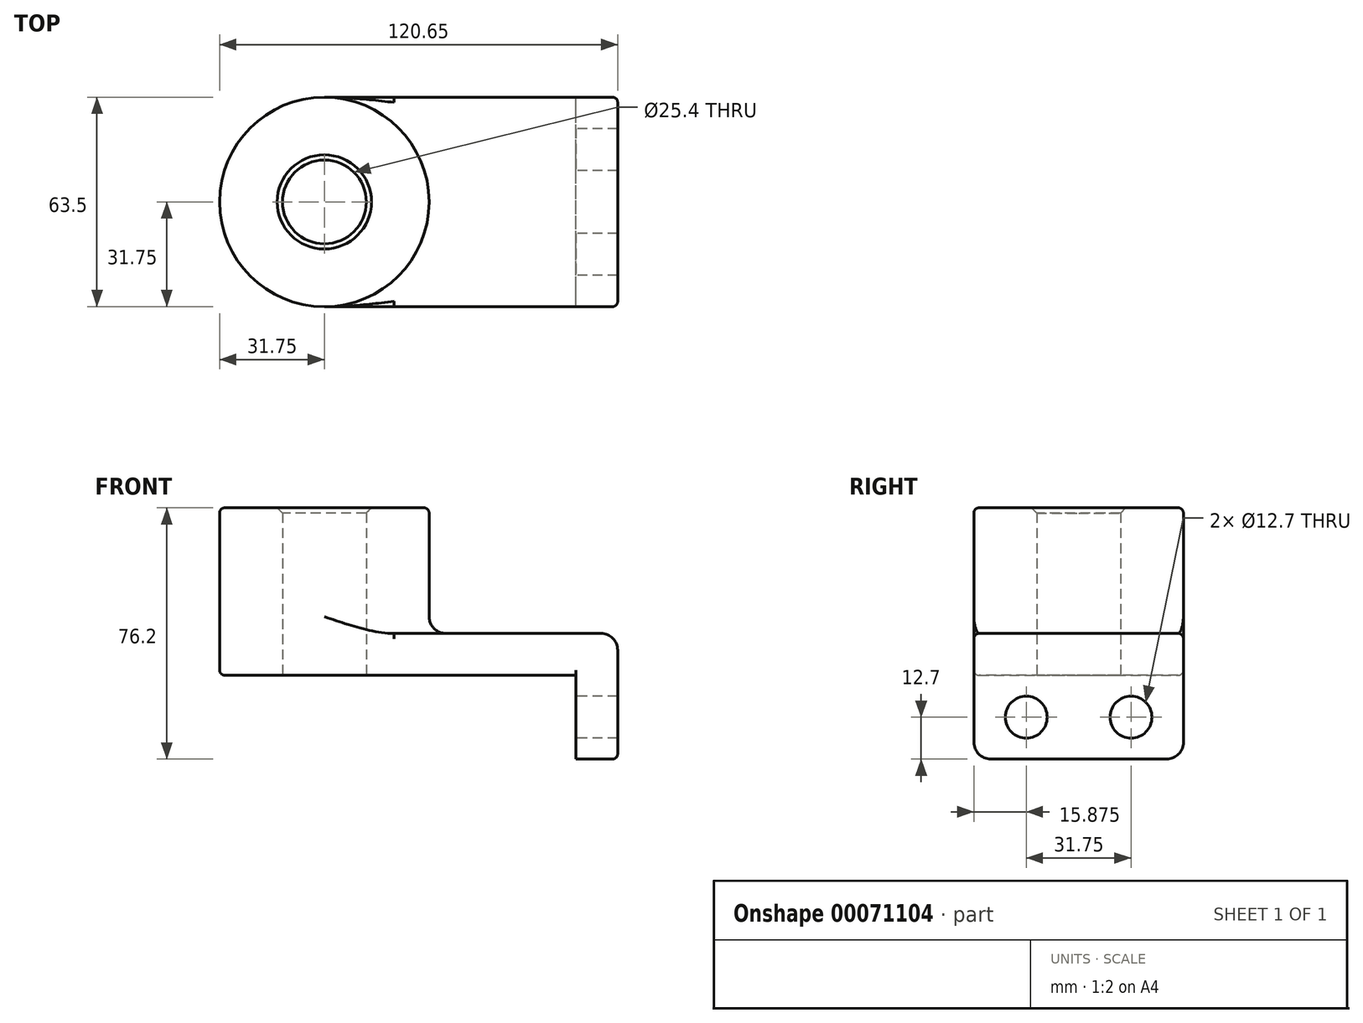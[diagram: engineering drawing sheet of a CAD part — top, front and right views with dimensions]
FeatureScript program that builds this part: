
annotation { "Feature Type Name" : "Feature", "Feature Type Description" : "" }
export const myFeature = defineFeature(function(context is Context, id is Id, definition is map)
    precondition{}
    {
        {
            var Q0;
            Q0=qCreatedBy(makeId("Top.planeOp"),FACE);
            var sketch = newSketch(context, id + "F0", { "sketchPlane" : qUnion([Q0])});
            skLineSegment(sketch, "E0.rect.bottom", {"start": v(38.1, -31.75) * mm, "end": v(-38.1, -31.75) * mm});
            skLineSegment(sketch, "E0.rect.top", {"start": v(38.1, 31.75) * mm, "end": v(-38.1, 31.75) * mm});
            skLineSegment(sketch, "E0.rect.left", {"start": v(38.1, -31.75) * mm, "end": v(38.1, 31.75) * mm});
            skLineSegment(sketch, "E0.rect.right", {"start": v(-38.1, -31.75) * mm, "end": v(-38.1, 31.75) * mm});
            skPoint(sketch, "E0.rect.middle", {"position": v(0, 0) * mm});
            skCircle(sketch, "E1", {"center": v(-38.1, 0) * mm, "radius": 31.75 * mm});
            skCircle(sketch, "E2", {"center": v(-38.1, 0) * mm, "radius": 12.7 * mm});
            skSolve(sketch);
        }
        {
            var Q0;
            Q0 = qSketchRegion(id + "F0", true);
            extrude(context, id + "F1", {"entities" : qUnion([Q0]), "depth" : 12.7 * mm});
        }
        {
            var Q0;
            {var subQ1=sQuery(id+"F0.wireOp",EDGE,"E0.rect.right");var subQ3=sQuery(id+"F0.wireOp",EDGE,"E2");var subQ4=makeQuery(id+"F0.imprint","INTERSECT",VERTEX,{"disambiguationData":[OD(0.0)],"derivedFrom":[subQ1,subQ3]});Q0=makeQuery(id+"F0.imprint","IMPRINT",FACE,{"disambiguationData":[TD([[makeQuery(id+"F0.imprint","IMPRINT",EDGE,{"disambiguationData":[TD([[subQ4,-1.0]])],"derivedFrom":subQ3}),-1.0]])]});}
            var Q1;
            {var subQ1=sQuery(id+"F0.wireOp",EDGE,"E0.rect.right");var subQ3=sQuery(id+"F0.wireOp",EDGE,"E2");var subQ4=makeQuery(id+"F0.imprint","INTERSECT",VERTEX,{"disambiguationData":[OD(0.0)],"derivedFrom":[subQ1,subQ3]});Q1=makeQuery(id+"F0.imprint","IMPRINT",FACE,{"disambiguationData":[TD([[makeQuery(id+"F0.imprint","IMPRINT",EDGE,{"disambiguationData":[TD([[subQ4,1.0]])],"derivedFrom":subQ3}),-1.0]])]});}
            extrude(context, id + "F2", {"entities" : qUnion([Q0, Q1]), "operationType" : NewBodyOperationType.ADD, "depth" : 50.8 * mm});
        }
        {
            var Q0;
            Q0=makeQuery(id+"F1.opExtrude","SWEPT_FACE",FACE,{"disambiguationData":[OSD([sQuery(id+"F0.wireOp",EDGE,"E0.rect.left")])]});
            var sketch = newSketch(context, id + "F3", { "sketchPlane" : qUnion([Q0])});
            skLineSegment(sketch, "E3.bottom", {"start": v(-31.75, 12.7) * mm, "end": v(31.75, 12.7) * mm});
            skLineSegment(sketch, "E3.top", {"start": v(-31.75, -25.4) * mm, "end": v(31.75, -25.4) * mm});
            skLineSegment(sketch, "E3.left", {"start": v(-31.75, 12.7) * mm, "end": v(-31.75, -25.4) * mm});
            skLineSegment(sketch, "E3.right", {"start": v(31.75, 12.7) * mm, "end": v(31.75, -25.4) * mm});
            skLineSegment(sketch, "E4", {"start": v(0, 0) * mm, "end": v(0, -25.4) * mm});
            skCircle(sketch, "E5", {"center": v(-15.87, -12.7) * mm, "radius": 6.35 * mm});
            skCircle(sketch, "E6.MirrorC", {"center": v(15.88, -12.7) * mm, "radius": 6.35 * mm});
            skSolve(sketch);
        }
        {
            var Q0;
            Q0 = qSketchRegion(id + "F3", true);
            extrude(context, id + "F4", {"entities" : qUnion([Q0]), "operationType" : NewBodyOperationType.ADD, "depth" : 12.7 * mm});
        }
        {
            var Q0;
            Q0=makeQuery(id+"F4.opExtrude","CAP_EDGE",EDGE,{"disambiguationData":[OSD([sQuery(id+"F3.wireOp",EDGE,"E3.bottom")])],"isStart":false});
            var Q1;
            {var subQ0=sQuery(id+"F0.wireOp",EDGE,"E1");Q1=makeQuery(id+"F2.boolean.opBoolean","INTERSECT",EDGE,{"derivedFrom":[makeQuery(id+"F1.opExtrude","CAP_FACE",FACE,{"disambiguationData":[OSD([sQuery(id+"F0.wireOp",EDGE,"E0.rect.bottom"),sQuery(id+"F0.wireOp",EDGE,"E0.rect.top"),sQuery(id+"F0.wireOp",EDGE,"E0.rect.left"),subQ0,sQuery(id+"F0.wireOp",EDGE,"E2")])],"isStart":false}),makeQuery(id+"F2.opExtrude","SWEPT_FACE",FACE,{"disambiguationData":[OSD([subQ0])]})]});}
            var Q2;
            Q2=makeQuery(id+"F4.opExtrude","SWEPT_EDGE",EDGE,{"disambiguationData":[OSD([sQuery(id+"F3.wireOp",EDGE,"E3.top"),sQuery(id+"F3.wireOp",EDGE,"E3.left")])]});
            var Q3;
            Q3=makeQuery(id+"F4.opExtrude","SWEPT_EDGE",EDGE,{"disambiguationData":[OSD([sQuery(id+"F3.wireOp",EDGE,"E3.top"),sQuery(id+"F3.wireOp",EDGE,"E3.right")])]});
            var Q4;
            Q4=makeQuery(id+"F1.opExtrude","CAP_EDGE",EDGE,{"disambiguationData":[OSD([sQuery(id+"F0.wireOp",EDGE,"E0.rect.left")])],"isStart":true});
            fillet(context, id + "F5", {"entities" : qUnion([Q0, Q1, Q2, Q3, Q4]), "radius" : 5.08 * mm, "tangentPropagation" : true, "allowEdgeOverflow" : false});
        }
        {
            var Q0;
            Q0=makeQuery(id+"F4.boolean.opBoolean","MERGE",EDGE,{"derivedFrom":[makeQuery(id+"F1.opExtrude","CAP_EDGE",EDGE,{"disambiguationData":[OSD([sQuery(id+"F0.wireOp",EDGE,"E0.rect.bottom")])],"isStart":false}),makeQuery(id+"F4.opExtrude","SWEPT_EDGE",EDGE,{"disambiguationData":[OSD([sQuery(id+"F3.wireOp",EDGE,"E3.bottom"),sQuery(id+"F3.wireOp",EDGE,"E3.left")])]})]});
            var Q1;
            Q1=makeQuery(id+"F1.opExtrude","CAP_EDGE",EDGE,{"disambiguationData":[OSD([sQuery(id+"F0.wireOp",EDGE,"E0.rect.bottom")])],"isStart":true});
            var Q2;
            Q2=makeQuery(id+"F2.opExtrude","CAP_EDGE",EDGE,{"disambiguationData":[OSD([sQuery(id+"F0.wireOp",EDGE,"E1")])],"isStart":false});
            fillet(context, id + "F6", {"entities" : qUnion([Q0, Q1, Q2]), "radius" : 1.59 * mm, "tangentPropagation" : true, "allowEdgeOverflow" : false});
        }
        {
            var Q0;
            Q0=makeQuery(id+"F2.opExtrude","CAP_EDGE",EDGE,{"disambiguationData":[OSD([sQuery(id+"F0.wireOp",EDGE,"E2")])],"isStart":false});
            chamfer(context, id + "F7", {"entities" : qUnion([Q0]), "width" : 1.59 * mm, "tangentPropagation" : true});
        }
    });
